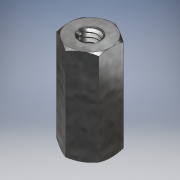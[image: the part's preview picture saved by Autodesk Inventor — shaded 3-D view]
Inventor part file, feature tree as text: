
AUTODESK INVENTOR PART (.ipt)
format: ipt  version: 2017 (Build 210142000, 142)  size: 826,368 bytes
history: native  units: mm
features: other x1, mirror x1
ambient origin geometry x8: Origin, YZ Plane, XZ Plane, XY Plane, X Axis, Y Axis, Z Axis, Center Point
bodies: Body1 (feature_tree)
feature tree (2):
  other  "Sólido1"
  mirror  "Mirror1"
